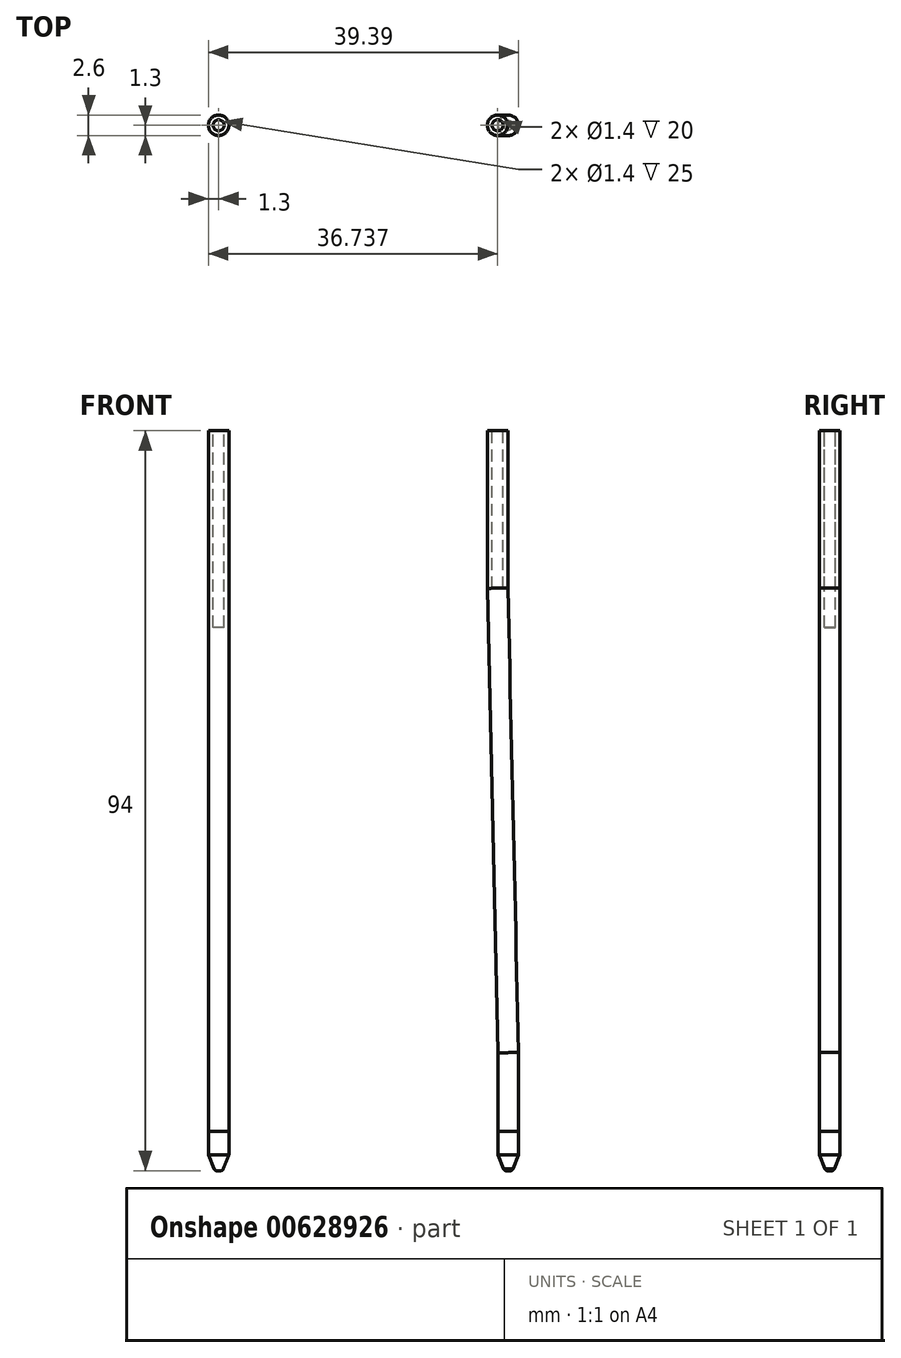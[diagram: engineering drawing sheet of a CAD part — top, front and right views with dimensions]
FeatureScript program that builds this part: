
annotation { "Feature Type Name" : "Feature", "Feature Type Description" : "" }
export const myFeature = defineFeature(function(context is Context, id is Id, definition is map)
    precondition{}
    {
        {
            var Q0;
            Q0=qCreatedBy(makeId("Top.planeOp"),FACE);
            var sketch = newSketch(context, id + "F0", { "sketchPlane" : qUnion([Q0])});
            skCircle(sketch, "E0", {"center": v(0, 0) * mm, "radius": 1.3 * mm});
            skSolve(sketch);
        }
        {
            var Q0;
            Q0=makeQuery(id+"F0.imprint","IMPRINT",FACE,{"disambiguationData":[TD([[makeQuery(id+"F0.imprint","IMPRINT",EDGE,{"derivedFrom":sQuery(id+"F0.wireOp",EDGE,"E0")}),1.0]])]});
            extrude(context, id + "F1", {"entities" : qUnion([Q0]), "endBound" : BoundingType.SYMMETRIC, "depth" : 89 * mm, "offsetDistance" : 25 * mm});
        }
        {
            var Q0;
            Q0=makeQuery(id+"F1.opExtrude","CAP_FACE",FACE,{"disambiguationData":[OSD([sQuery(id+"F0.wireOp",EDGE,"E0")])],"isStart":true});
            extrude(context, id + "F2", {"entities" : qUnion([Q0]), "depth" : 5 * mm, "offsetDistance" : 25 * mm});
        }
        {
            var Q0;
            Q0=qCreatedBy(makeId("Front.planeOp"),FACE);
            var sketch = newSketch(context, id + "F3", { "sketchPlane" : qUnion([Q0])});
            skLineSegment(sketch, "E1", {"start": v(-39.78, 44.5) * mm, "end": v(53.38, 44.5) * mm, "construction": true});
            skLineSegment(sketch, "E2", {"start": v(-41.32, -44.5) * mm, "end": v(63.52, -44.5) * mm, "construction": true});
            skLineSegment(sketch, "E3", {"start": v(18.68, 39.87) * mm, "end": v(18.68, -39.56) * mm, "construction": true});
            skLineSegment(sketch, "E4", {"start": v(35.97, 54.5) * mm, "end": v(35.97, 24.5) * mm});
            skLineSegment(sketch, "E5", {"start": v(35.97, 24.5) * mm, "end": v(37.32, -34.5) * mm});
            skLineSegment(sketch, "E6", {"start": v(37.32, -34.5) * mm, "end": v(37.32, -54.5) * mm});
            skLineSegment(sketch, "E7", {"start": v(-44.37, 54.5) * mm, "end": v(93.01, 54.5) * mm, "construction": true});
            skLineSegment(sketch, "E8", {"start": v(-50.56, -54.5) * mm, "end": v(86.35, -54.5) * mm, "construction": true});
            skLineSegment(sketch, "E9.bottom", {"start": v(23.68, -44.5) * mm, "end": v(43.68, -44.5) * mm});
            skLineSegment(sketch, "E9.top", {"start": v(23.68, -62.5) * mm, "end": v(43.68, -62.5) * mm});
            skLineSegment(sketch, "E9.left", {"start": v(23.68, -44.5) * mm, "end": v(23.68, -62.5) * mm});
            skLineSegment(sketch, "E9.right", {"start": v(43.68, -44.5) * mm, "end": v(43.68, -62.5) * mm});
            skLineSegment(sketch, "E10.bottom", {"start": v(23.68, 44.5) * mm, "end": v(43.68, 44.5) * mm});
            skLineSegment(sketch, "E10.top", {"start": v(23.68, 62.7) * mm, "end": v(43.68, 62.7) * mm});
            skLineSegment(sketch, "E10.left", {"start": v(23.68, 44.5) * mm, "end": v(23.68, 62.7) * mm});
            skLineSegment(sketch, "E10.right", {"start": v(43.68, 44.5) * mm, "end": v(43.68, 62.7) * mm});
            skSolve(sketch);
        }
        {
            var Q0;
            Q0=qCreatedBy(makeId("Top.planeOp"),FACE);
            var sketch = newSketch(context, id + "F4", { "sketchPlane" : qUnion([Q0])});
            skCircle(sketch, "E11", {"center": v(36, 0) * mm, "radius": 1.3 * mm});
            skSolve(sketch);
        }
        {
            var Q0;
            Q0=makeQuery(id+"F4.imprint","IMPRINT",FACE,{"disambiguationData":[TD([[makeQuery(id+"F4.imprint","IMPRINT",EDGE,{"derivedFrom":sQuery(id+"F4.wireOp",EDGE,"E11")}),1.0]])]});
            var Q1;
            Q1=sQuery(id+"F3.wireOp",EDGE,"E4");
            var Q2;
            Q2=sQuery(id+"F3.wireOp",EDGE,"E5");
            var Q3;
            Q3=sQuery(id+"F3.wireOp",EDGE,"E6");
            sweep(context, id + "F5", {"profiles" : qUnion([Q0]), "path" : qUnion([Q1, Q2, Q3])});
        }
        {
            var Q0;
            Q0=makeQuery(id+"F3.imprint","IMPRINT",FACE,{"disambiguationData":[TD([[makeQuery(id+"F3.imprint","IMPRINT",EDGE,{"derivedFrom":sQuery(id+"F3.wireOp",EDGE,"E10.top")}),-1.0]])]});
            var Q1;
            Q1=makeQuery(id+"F3.imprint","IMPRINT",FACE,{"disambiguationData":[TD([[makeQuery(id+"F3.imprint","IMPRINT",EDGE,{"derivedFrom":sQuery(id+"F3.wireOp",EDGE,"E9.top")}),1.0]])]});
            extrude(context, id + "F6", {"entities" : qUnion([Q0, Q1]), "operationType" : NewBodyOperationType.REMOVE, "endBound" : BoundingType.SYMMETRIC, "oppositeDirection" : true, "depth" : 25 * mm, "offsetDistance" : 25 * mm});
        }
        {
            var Q0;
            Q0=makeQuery(id+"F6.boolean.opBoolean","COPY",FACE,{"derivedFrom":makeQuery(id+"F6.opExtrude","SWEPT_FACE",FACE,{"disambiguationData":[OSD([sQuery(id+"F3.wireOp",EDGE,"E9.bottom")])]})});
            extrude(context, id + "F7", {"entities" : qUnion([Q0]), "depth" : 5 * mm, "offsetDistance" : 25 * mm});
        }
        {
            var Q0;
            Q0=makeQuery(id+"F2.opExtrude","CAP_EDGE",EDGE,{"disambiguationData":[OSD([sQuery(id+"F0.wireOp",EDGE,"E0")])],"isStart":false});
            var Q1;
            Q1=makeQuery(id+"F7.opExtrude","CAP_FACE",FACE,{"disambiguationData":[OSD([sQuery(id+"F3.wireOp",EDGE,"E9.bottom")])],"isStart":false});
            chamfer(context, id + "F8", {"entities" : qUnion([Q0, Q1]), "chamferType" : ChamferType.TWO_OFFSETS, "width1" : .8 * mm, "oppositeDirection" : true, "width2" : 2 * mm, "tangentPropagation" : true});
        }
        {
            var Q0;
            {var subQ0=sQuery(id+"F0.wireOp",EDGE,"E0");Q0=makeQuery(id+"F8.opChamfer","BLEND_EDGE",EDGE,{"blendedFrom":[makeQuery(id+"F2.opExtrude","CAP_EDGE",EDGE,{"disambiguationData":[OSD([subQ0])],"isStart":false}),makeQuery(id+"F2.opExtrude","CAP_FACE",FACE,{"disambiguationData":[OSD([subQ0])],"isStart":false})],"blendedInto":[makeQuery(id+"F2.opExtrude","CAP_FACE",FACE,{"disambiguationData":[OSD([subQ0])],"isStart":false})]});}
            var Q1;
            {var subQ0=sQuery(id+"F3.wireOp",EDGE,"E9.bottom");Q1=makeQuery(id+"F8.opChamfer","BLEND_EDGE",EDGE,{"blendedFrom":[makeQuery(id+"F7.opExtrude","CAP_EDGE",EDGE,{"disambiguationData":[OSD([sQuery(id+"F3.wireOp",EDGE,"E6"),subQ0,sQuery(id+"F4.wireOp",EDGE,"E11")])],"isStart":false}),makeQuery(id+"F7.opExtrude","CAP_FACE",FACE,{"disambiguationData":[OSD([subQ0])],"isStart":false})],"blendedInto":[makeQuery(id+"F7.opExtrude","CAP_FACE",FACE,{"disambiguationData":[OSD([subQ0])],"isStart":false})]});}
            fillet(context, id + "F9", {"entities" : qUnion([Q0, Q1]), "radius" : 0.35 * mm, "tangentPropagation" : true, "allowEdgeOverflow" : false});
        }
        {
            var Q0;
            Q0=makeQuery(id+"F1.opExtrude","CAP_FACE",FACE,{"disambiguationData":[OSD([sQuery(id+"F0.wireOp",EDGE,"E0")])],"isStart":false});
            var sketch = newSketch(context, id + "F10", { "sketchPlane" : qUnion([Q0])});
            skCircle(sketch, "E12", {"center": v(0, 0) * mm, "radius": 0.7 * mm});
            skSolve(sketch);
        }
        {
            var Q0;
            Q0=qSketchRegion(id+"F10",true);
            extrude(context, id + "F11", {"entities" : qUnion([Q0]), "operationType" : NewBodyOperationType.REMOVE, "oppositeDirection" : true, "depth" : 25 * mm, "offsetDistance" : 25 * mm});
        }
        {
            var Q0;
            Q0=makeQuery(id+"F6.boolean.opBoolean","COPY",FACE,{"derivedFrom":makeQuery(id+"F6.opExtrude","SWEPT_FACE",FACE,{"disambiguationData":[OSD([sQuery(id+"F3.wireOp",EDGE,"E10.bottom")])]})});
            var sketch = newSketch(context, id + "F12", { "sketchPlane" : qUnion([Q0])});
            skCircle(sketch, "E13", {"center": v(35.44, 0) * mm, "radius": 0.7 * mm});
            skSolve(sketch);
        }
        {
            var Q0;
            Q0=makeQuery(id+"F12.imprint","IMPRINT",FACE,{"disambiguationData":[TD([[makeQuery(id+"F12.imprint","IMPRINT",EDGE,{"derivedFrom":sQuery(id+"F12.wireOp",EDGE,"E13")}),1.0]])]});
            extrude(context, id + "F13", {"entities" : qUnion([Q0]), "operationType" : NewBodyOperationType.REMOVE, "oppositeDirection" : true, "depth" : 20 * mm, "offsetDistance" : 25 * mm});
        }
    });
